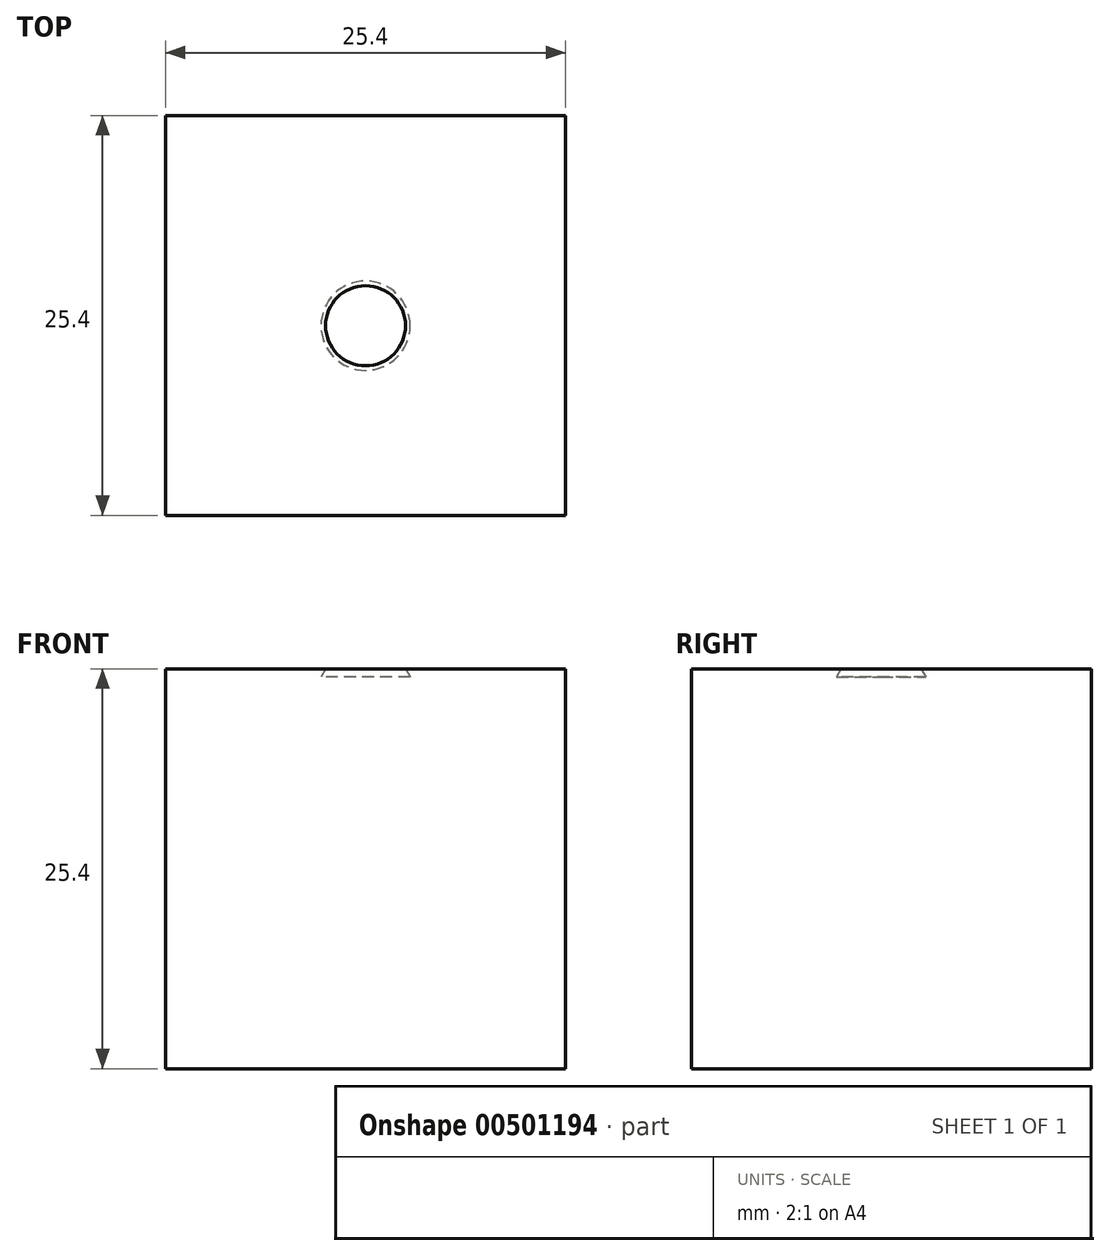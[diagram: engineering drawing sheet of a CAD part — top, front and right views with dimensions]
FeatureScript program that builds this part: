
annotation { "Feature Type Name" : "Feature", "Feature Type Description" : "" }
export const myFeature = defineFeature(function(context is Context, id is Id, definition is map)
    precondition{}
    {
        {
            var Q0;
            Q0=qCreatedBy(makeId("Front.planeOp"),FACE);
            var sketch = newSketch(context, id + "F0", { "sketchPlane" : qUnion([Q0])});
            skLineSegment(sketch, "E0.bottom", {"start": v(12.7, 12.7) * mm, "end": v(-12.7, 12.7) * mm});
            skLineSegment(sketch, "E0.top", {"start": v(12.7, -12.7) * mm, "end": v(-12.7, -12.7) * mm});
            skLineSegment(sketch, "E0.left", {"start": v(12.7, 12.7) * mm, "end": v(12.7, -12.7) * mm});
            skLineSegment(sketch, "E0.right", {"start": v(-12.7, 12.7) * mm, "end": v(-12.7, -12.7) * mm});
            skPoint(sketch, "E0.middle", {"position": v(0, 0) * mm});
            skSolve(sketch);
        }
        {
            var Q0;
            Q0=makeQuery(id+"F0.imprint","IMPRINT",FACE,{"disambiguationData":[TD([[makeQuery(id+"F0.imprint","IMPRINT",EDGE,{"derivedFrom":sQuery(id+"F0.wireOp",EDGE,"E0.bottom")}),1.0]])]});
            extrude(context, id + "F1", {"entities" : qUnion([Q0]), "depth" : 25.4 * mm});
        }
        {
            var Q0;
            Q0=makeQuery(id+"F1.opExtrude","SWEPT_FACE",FACE,{"disambiguationData":[OSD([sQuery(id+"F0.wireOp",EDGE,"E0.bottom")])]});
            var sketch = newSketch(context, id + "F2", { "sketchPlane" : qUnion([Q0])});
            skCircle(sketch, "E1", {"center": v(0, -13.36) * mm, "radius": 2.54 * mm});
            skSolve(sketch);
        }
        {
            var Q0;
            Q0=makeQuery(id+"F2.imprint","IMPRINT",FACE,{"disambiguationData":[TD([[makeQuery(id+"F2.imprint","IMPRINT",EDGE,{"derivedFrom":sQuery(id+"F2.wireOp",EDGE,"E1")}),1.0]])]});
            extrude(context, id + "F3", {"entities" : qUnion([Q0]), "operationType" : NewBodyOperationType.REMOVE, "oppositeDirection" : true, "depth" : 0.5 * mm, "hasDraft" : true, "draftAngle" : 30 * degree});
        }
    });
